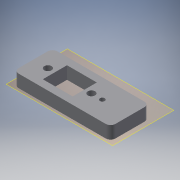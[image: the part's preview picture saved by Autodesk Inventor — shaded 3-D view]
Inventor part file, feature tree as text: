
AUTODESK INVENTOR PART (.ipt)
format: ipt  version: 2016 SP1 (Build 200210100, 210)  size: 172,032 bytes
history: native  units: mm
features: sketch x3, extrude x3, reference x2, plane x1
ambient origin geometry x8: Origin, YZ Plane, XZ Plane, XY Plane, X Axis, Y Axis, Z Axis, Center Point
bodies: Solid1 (feature_tree)
feature tree (9):
  plane  "Work Plane1"
  sketch  "Sketch1"  dims[d2=6.0mm d3=12.684184mm]
  extrude  "Extrusion4"  Depth=12.684184mm
  extrude  "Extrusion5"  Depth=7.0mm
  extrude  "Extrusion6"  Depth=6.0mm
  sketch  "Sketch5"  dims[d4=2.0mm d5=7.0mm]
  reference  "Reference11"
  reference  "Reference12"
  sketch  "Sketch6"  dims[d14=5.2mm d15=0.0mm d16=6.0mm d17=7.0mm d18=3.0mm d19=0.0mm d20=3.0mm d21=0.0mm d22=4.0mm d23=4.0mm]
